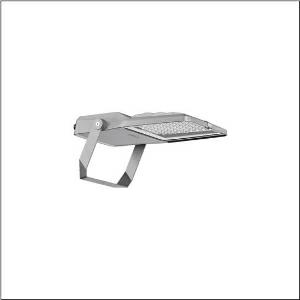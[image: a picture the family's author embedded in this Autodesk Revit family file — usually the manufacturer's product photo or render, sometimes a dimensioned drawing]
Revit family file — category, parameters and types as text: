
# Revit family: floodlight_fl_21_iq_mini___rs12_5xa7772c3b1a_483e
name_source: partatom
category: Lighting Fixtures
units: mm (PartAtom-declared; Revit-internal decimal feet)

## family parameters
Cut with Voids When Loaded = No
Host = Face
Light Source = No
Part Type = Normal
Room Calculation Point = No
Round Connector Dimension = Use Diameter
Shared = No

## types (1)
- --- (1 x LED, 10620 lm, 87.2 W, 3000K)
    Apparent Load = 87 VA
    CIE Flux Codes = 79 92 99 100 100
    Color Rendering = 80
    Color Temperature = 3000K
    Default Elevation = 1800 mm
    Description = Floodlight FL 21 iQ mini, floodlight, primary light control with lens, of PMMA, primary optical cover: protective disc, of toughened safety glass, transparent, light distribution: RS12, light emission: direct distribution, installation type: surface-mounted, LED, High Power LED, rated luminous flux: 10.620lm, luminous efficacy: 122lm/W, light colour: 830, colour temperature: 3000K, control gear: iQ Street-Remote/DALI, control: Street-Remote, Auto-Match, Temp-Guard, Night-Set, Smart-Wire, Desk-Remote (wireless, voltage-free reading and setting of iQ features in the workshop via application-optimized NFC function/RFID function), optimised constant luminous flux control (CLO 2.0), with terminal, 6-pole, mains connection: 220..240V, AC, 50/60Hz, start of lifetime: 87W, end of service life: 92W, reduction: 40W, luminaire housing, of diecast aluminium, powder-coated, Siteco® metallic grey (DB 702S), corrosivity category C5 mid according to DIN EN ISO 12944, suitable for swimming pools, chlorine-resistant, sealing non-destructively replaceable, mounting bracket, of steel, galvanised, powder-coated, Siteco® metallic grey (DB 702S), protection rating (complete): IP66, insulation class (complete): insulation class II (safety insulation), certification: CE, ENEC, VDE, protection symbol: D, impact resistance: IK08, permissible operating ambient temperature: -40..+40°C, permissible operating ambient temperature for outdoor applications: -40..+50°C, standard: DIN EN 12944, LABS conformity tested according to VDMA 24364:2018-05, packaging unit: 1 piece

Light Distribution: RS12
    Height = 70 mm
    Lamp = 1 x LED
    Lamp Light Flux = 10620 lm
    Lamp Power = 87.2 W
    Lamp count = 1
    Length = 485 mm
    Luminous efficacy = 122 lm/W
    Manufacturer = Siteco
    ModVariant = No
    Model = 5XA7772C3B1A
    Number of Poles = 1
    OnlyDefault = Yes
    Power Factor = 1
    Product Name = Floodlight FL 21 iQ mini | RS12
    Product group = floodlight | pylon annexe
    ProductGroupID = 6200
    Protection Class = Protection class II
    Protection Degree = IP 66
    RLX_Detail_Level = 1
    RLX_Emergency_Light_Flux = 0 lm
    RLX_Emergency_Type = 0
    RLX_Emergency_Type_DB = No
    RlxData = <blob elided: 90829 chars, md5=42c57d3f>
    Socket = socket
    Standby Power = 0 W
    System Light Flux = 10620 lm
    System Power = 87 W
    Type Comments = factory setting: luminous flux: 100 % | dim-lin: 254 | 456 mA
    Type Image = l_1006845.jpg
    URL = http://relux.com
    VarID = @adj_167600
    Voltage = 0 V
    Weight = 0.00 kg
    Width = 337 mm

## geometry (parser evidence)
native form markers: Blend x4, Sweep x13
no freeform markers — native parametric forms only
